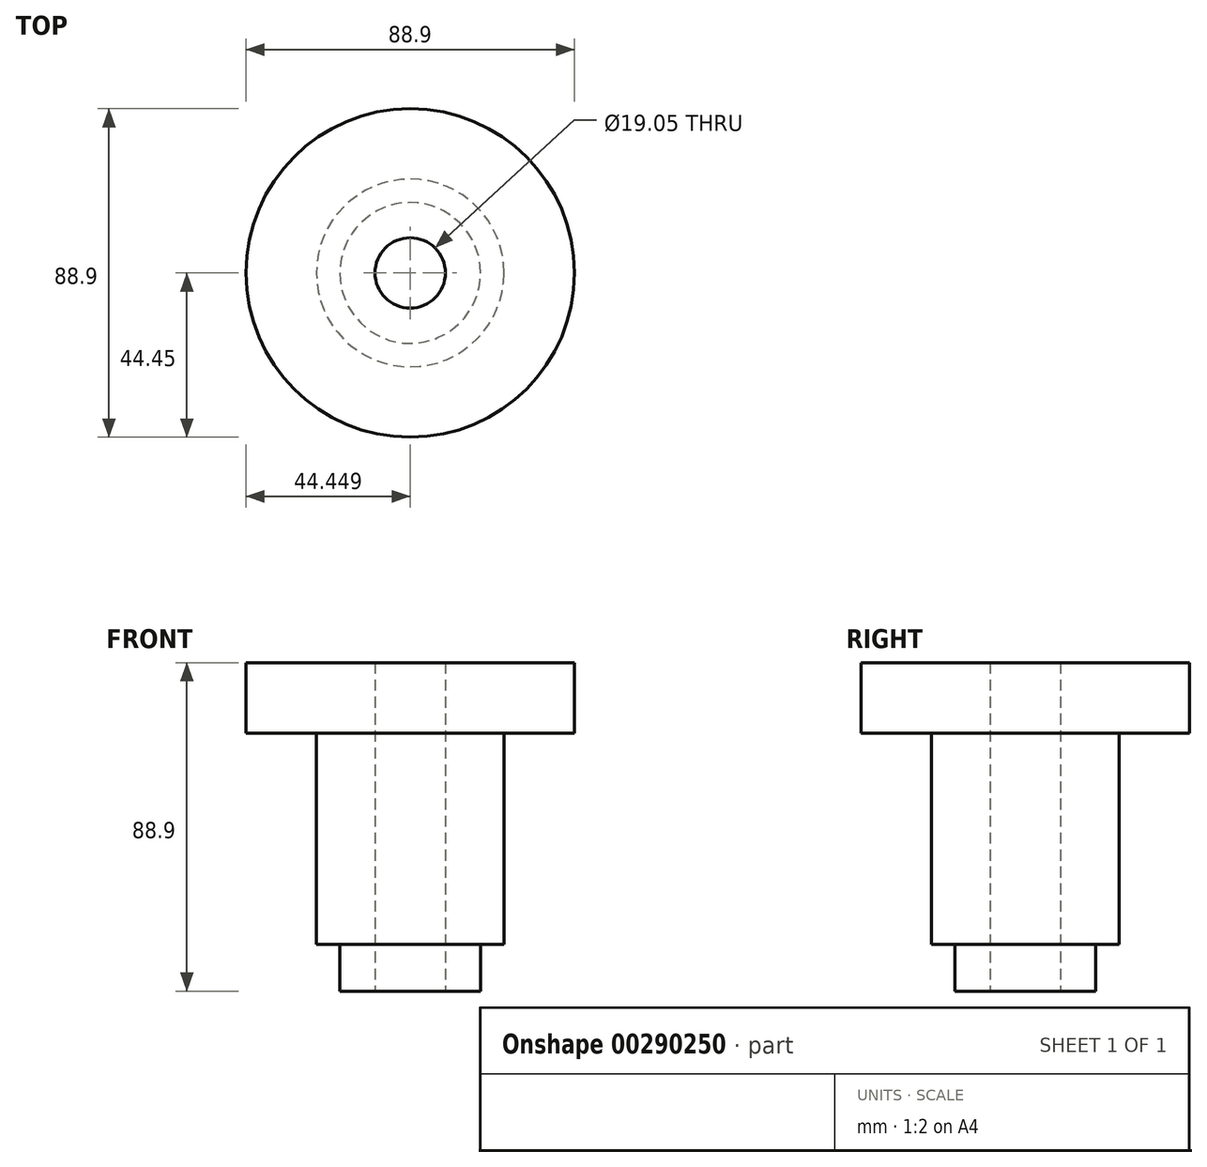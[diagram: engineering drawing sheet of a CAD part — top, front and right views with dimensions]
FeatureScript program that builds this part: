
annotation { "Feature Type Name" : "Feature", "Feature Type Description" : "" }
export const myFeature = defineFeature(function(context is Context, id is Id, definition is map)
    precondition{}
    {
        {
            var Q0;
            Q0=qCreatedBy(makeId("Front.planeOp"),FACE);
            var sketch = newSketch(context, id + "F0", { "sketchPlane" : qUnion([Q0])});
            skLineSegment(sketch, "E0.bottom", {"start": v(2.42, -91.43) * mm, "end": v(-16.63, -91.43) * mm});
            skLineSegment(sketch, "E0.top", {"start": v(2.42, -78.73) * mm, "end": v(-16.63, -78.73) * mm, "construction": true});
            skLineSegment(sketch, "E0.left", {"start": v(2.42, -91.43) * mm, "end": v(2.42, 98.35) * mm});
            skLineSegment(sketch, "E0.right", {"start": v(-16.63, -91.43) * mm, "end": v(-16.63, -78.73) * mm});
            skLineSegment(sketch, "E1", {"start": v(2.42, -21.58) * mm, "end": v(-22.98, -21.58) * mm, "construction": true});
            skLineSegment(sketch, "E2", {"start": v(-22.98, -21.58) * mm, "end": v(-22.98, -78.73) * mm});
            skLineSegment(sketch, "E3", {"start": v(2.42, -2.53) * mm, "end": v(-42.03, -2.53) * mm});
            skLineSegment(sketch, "E4", {"start": v(-42.03, -2.53) * mm, "end": v(-42.03, -21.58) * mm});
            skLineSegment(sketch, "E5", {"start": v(-16.63, -78.73) * mm, "end": v(-22.98, -78.73) * mm});
            skLineSegment(sketch, "E6", {"start": v(-22.98, -21.58) * mm, "end": v(-42.03, -21.58) * mm});
            skSolve(sketch);
        }
        {
            var Q0;
            {var subQ1=sQuery(id+"F0.wireOp",EDGE,"E0.bottom");Q0=makeQuery(id+"F0.imprint","IMPRINT",FACE,{"disambiguationData":[TD([[makeQuery(id+"F0.imprint","IMPRINT",EDGE,{"derivedFrom":subQ1}),-1.0]])]});}
            var Q1;
            Q1=sQuery(id+"F0.wireOp",EDGE,"E0.left");
            revolve(context, id + "F1", {"entities" : qUnion([Q0]), "axis" : qUnion([Q1]), "revolveType" : RevolveType.FULL});
        }
        {
            var Q0;
            Q0=makeQuery(id+"F1.opRevolve","SWEPT_FACE",FACE,{"disambiguationData":[OSD([sQuery(id+"F0.wireOp",EDGE,"E0.bottom")])]});
            var sketch = newSketch(context, id + "F2", { "sketchPlane" : qUnion([Q0])});
            skCircle(sketch, "E7", {"center": v(2.42, 0) * mm, "radius": 9.53 * mm});
            skSolve(sketch);
        }
        {
            var Q0;
            Q0=makeQuery(id+"F2.imprint","IMPRINT",FACE,{"disambiguationData":[TD([[makeQuery(id+"F2.imprint","IMPRINT",EDGE,{"derivedFrom":sQuery(id+"F2.wireOp",EDGE,"E7")}),1.0]])]});
            extrude(context, id + "F3", {"entities" : qUnion([Q0]), "operationType" : NewBodyOperationType.REMOVE, "oppositeDirection" : true, "depth" : 88.9 * mm});
        }
    });
